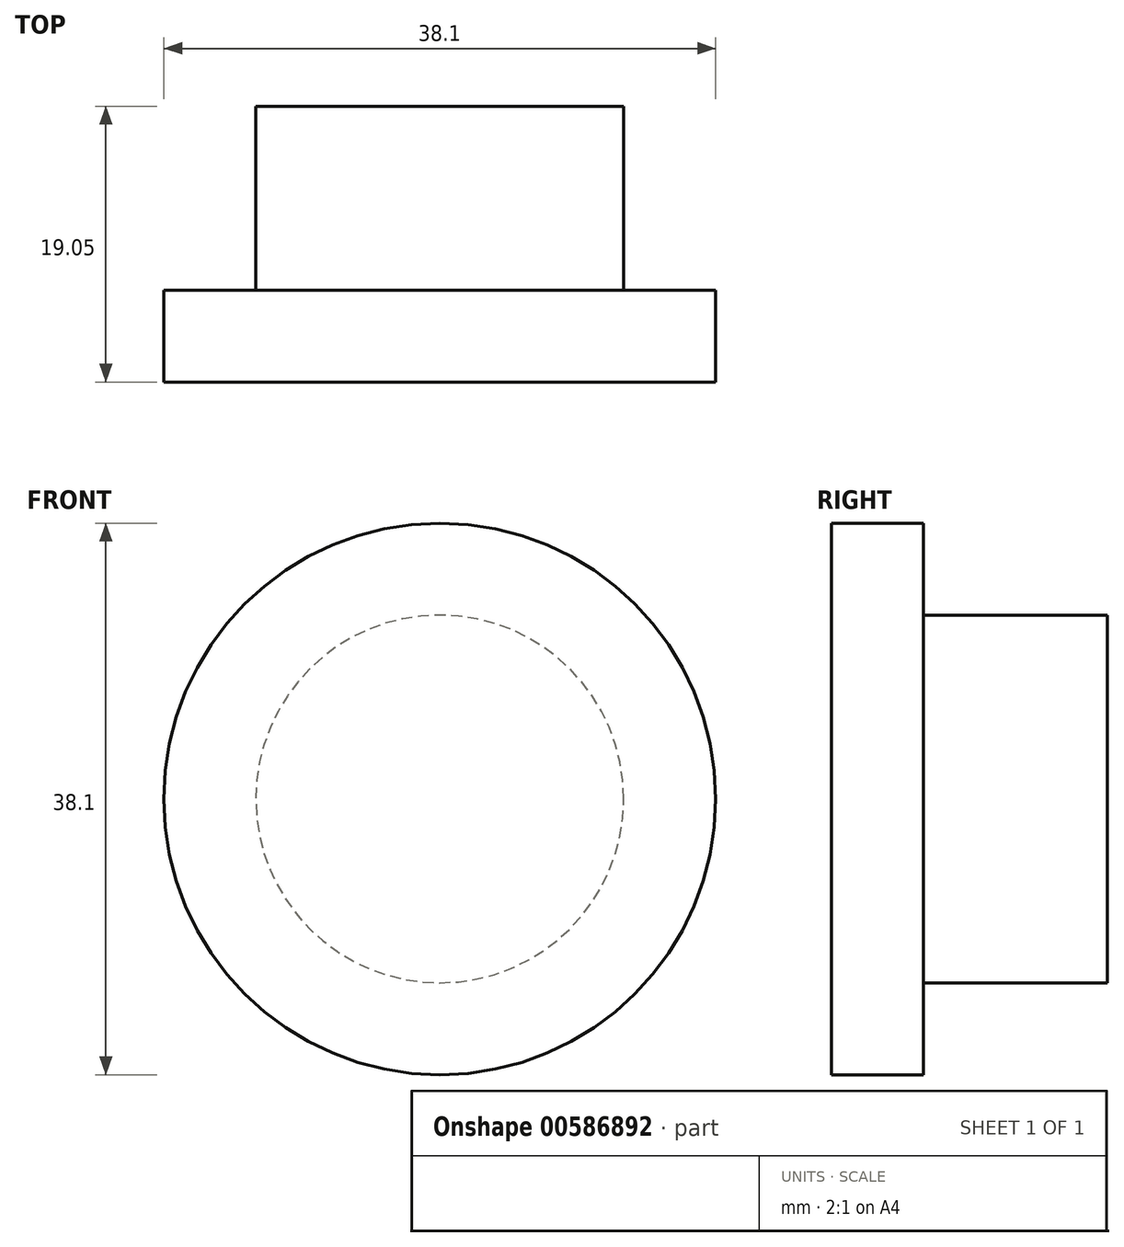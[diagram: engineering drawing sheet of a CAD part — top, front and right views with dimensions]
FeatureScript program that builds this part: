
annotation { "Feature Type Name" : "Feature", "Feature Type Description" : "" }
export const myFeature = defineFeature(function(context is Context, id is Id, definition is map)
    precondition{}
    {
        {
            var Q0;
            Q0=qCreatedBy(makeId("Front.planeOp"),FACE);
            var sketch = newSketch(context, id + "F0", { "sketchPlane" : qUnion([Q0])});
            skCircle(sketch, "E0", {"center": v(0, 0) * mm, "radius": 12.7 * mm});
            skSolve(sketch);
        }
        {
            var Q0;
            Q0=makeQuery(id+"F0.imprint","IMPRINT",FACE,{"disambiguationData":[TD([[makeQuery(id+"F0.imprint","IMPRINT",EDGE,{"derivedFrom":sQuery(id+"F0.wireOp",EDGE,"E0")}),1.0]])]});
            extrude(context, id + "F1", {"entities" : qUnion([Q0]), "depth" : 12.7 * mm, "offsetDistance" : 25.4 * mm});
        }
        {
            var Q0;
            Q0=makeQuery(id+"F1.opExtrude","CAP_FACE",FACE,{"disambiguationData":[OSD([sQuery(id+"F0.wireOp",EDGE,"E0")])],"isStart":false});
            var sketch = newSketch(context, id + "F2", { "sketchPlane" : qUnion([Q0])});
            skCircle(sketch, "E1", {"center": v(0, 0) * mm, "radius": 19.05 * mm});
            skSolve(sketch);
        }
        {
            var Q0;
            Q0=makeQuery(id+"F2.imprint","IMPRINT",FACE,{"disambiguationData":[TD([[makeQuery(id+"F2.imprint","IMPRINT",EDGE,{"derivedFrom":sQuery(id+"F2.wireOp",EDGE,"E1")}),1.0]])]});
            var Q1;
            Q1=makeQuery(id+"F2.imprint","IMPRINT",FACE,{"disambiguationData":[TD([[makeQuery(id+"F2.imprint","IMPRINT",EDGE,{"derivedFrom":makeQuery(id+"F1.opExtrude","CAP_EDGE",EDGE,{"disambiguationData":[OSD([sQuery(id+"F0.wireOp",EDGE,"E0")])],"isStart":false})}),1.0]])]});
            extrude(context, id + "F3", {"entities" : qUnion([Q0, Q1]), "depth" : 6.35 * mm, "offsetDistance" : 25.4 * mm});
        }
    });
